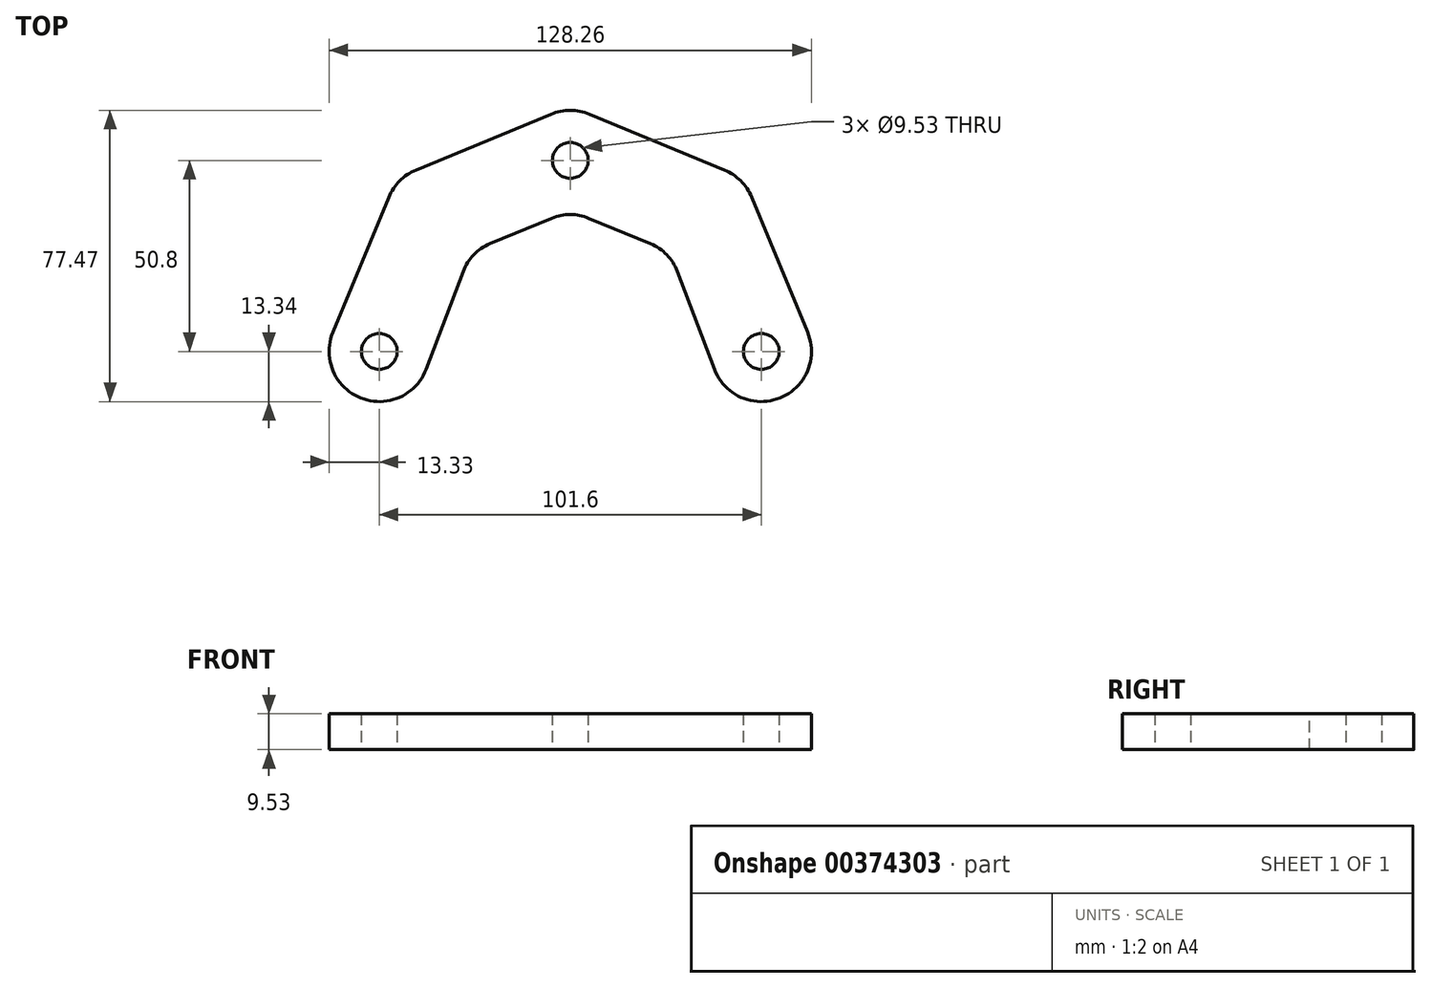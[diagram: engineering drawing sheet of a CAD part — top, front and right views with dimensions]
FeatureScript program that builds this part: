
annotation { "Feature Type Name" : "Feature", "Feature Type Description" : "" }
export const myFeature = defineFeature(function(context is Context, id is Id, definition is map)
    precondition{}
    {
        {
            var Q0;
            Q0=qCreatedBy(makeId("Top.planeOp"),FACE);
            var sketch = newSketch(context, id + "F0", { "sketchPlane" : qUnion([Q0])});
            skCircle(sketch, "E0", {"center": v(0, 0) * mm, "radius": 50.8 * mm, "construction": true});
            skLineSegment(sketch, "E1", {"start": v(0, 0) * mm, "end": v(-50.8, 0) * mm, "construction": true});
            skLineSegment(sketch, "E2", {"start": v(0, 0) * mm, "end": v(50.8, 0) * mm, "construction": true});
            skLineSegment(sketch, "E3", {"start": v(0, 37.47) * mm, "end": v(0, 50.8) * mm, "construction": true});
            skLineSegment(sketch, "E4", {"start": v(0, 0) * mm, "end": v(0, -50.8) * mm, "construction": true});
            skCircle(sketch, "E5", {"center": v(-50.8, 0) * mm, "radius": 13.34 * mm});
            skCircle(sketch, "E6", {"center": v(50.8, 0) * mm, "radius": 13.34 * mm});
            skCircle(sketch, "E7", {"center": v(50.8, 0) * mm, "radius": 4.76 * mm});
            skCircle(sketch, "E8", {"center": v(-50.8, 0) * mm, "radius": 4.76 * mm});
            skCircle(sketch, "E9", {"center": v(0, 50.8) * mm, "radius": 13.34 * mm});
            skCircle(sketch, "E10", {"center": v(0, 50.8) * mm, "radius": 4.76 * mm});
            skLineSegment(sketch, "E11", {"start": v(-26.5, 26.5) * mm, "end": v(-35.92, 35.92) * mm, "construction": true});
            skLineSegment(sketch, "E12", {"start": v(26.5, 26.5) * mm, "end": v(35.92, 35.92) * mm, "construction": true});
            skCircle(sketch, "E13", {"center": v(-35.92, 35.92) * mm, "radius": 13.34 * mm});
            skCircle(sketch, "E14", {"center": v(35.92, 35.92) * mm, "radius": 13.34 * mm});
            skLineSegment(sketch, "E15", {"start": v(63.12, 5.1) * mm, "end": v(48.24, 41.02) * mm});
            skLineSegment(sketch, "E16", {"start": v(5.1, 63.12) * mm, "end": v(41.02, 48.24) * mm});
            skLineSegment(sketch, "E17", {"start": v(-5.1, 63.12) * mm, "end": v(-41.02, 48.24) * mm});
            skLineSegment(sketch, "E18", {"start": v(-48.24, 41.02) * mm, "end": v(-63.12, 5.1) * mm});
            skLineSegment(sketch, "E19", {"start": v(-26.5, 26.5) * mm, "end": v(-38.33, -4.73) * mm});
            skLineSegment(sketch, "E20", {"start": v(-26.5, 26.5) * mm, "end": v(0, 37.47) * mm});
            skLineSegment(sketch, "E21", {"start": v(0, 37.47) * mm, "end": v(26.5, 26.5) * mm});
            skLineSegment(sketch, "E22", {"start": v(26.5, 26.5) * mm, "end": v(38.33, -4.73) * mm});
            skSolve(sketch);
        }
        {
            var Q0;
            Q0=makeQuery(id+"F0.imprint","IMPRINT",FACE,{"disambiguationData":[TD([[makeQuery(id+"F0.imprint","IMPRINT",EDGE,{"derivedFrom":sQuery(id+"F0.wireOp",EDGE,"E8")}),-1.0]])]});
            var Q1;
            {var subQ0=sQuery(id+"F0.wireOp",EDGE,"E18");Q1=makeQuery(id+"F0.imprint","IMPRINT",FACE,{"disambiguationData":[TD([[makeQuery(id+"F0.imprint","IMPRINT",EDGE,{"derivedFrom":subQ0}),1.0]])]});}
            var Q2;
            {var subQ0=sQuery(id+"F0.wireOp",EDGE,"E13");var subQ1=makeQuery(id+"F0.imprint","INTERSECT",VERTEX,{"derivedFrom":[subQ0,sQuery(id+"F0.wireOp",EDGE,"E17")]});Q2=makeQuery(id+"F0.imprint","IMPRINT",FACE,{"disambiguationData":[TD([[makeQuery(id+"F0.imprint","IMPRINT",EDGE,{"disambiguationData":[TD([[subQ1,-1.0]])],"derivedFrom":subQ0}),1.0]])]});}
            var Q3;
            {var subQ0=sQuery(id+"F0.wireOp",EDGE,"E17");Q3=makeQuery(id+"F0.imprint","IMPRINT",FACE,{"disambiguationData":[TD([[makeQuery(id+"F0.imprint","IMPRINT",EDGE,{"derivedFrom":subQ0}),1.0]])]});}
            var Q4;
            Q4=makeQuery(id+"F0.imprint","IMPRINT",FACE,{"disambiguationData":[TD([[makeQuery(id+"F0.imprint","IMPRINT",EDGE,{"derivedFrom":sQuery(id+"F0.wireOp",EDGE,"E10")}),-1.0]])]});
            var Q5;
            {var subQ0=sQuery(id+"F0.wireOp",EDGE,"E16");Q5=makeQuery(id+"F0.imprint","IMPRINT",FACE,{"disambiguationData":[TD([[makeQuery(id+"F0.imprint","IMPRINT",EDGE,{"derivedFrom":subQ0}),-1.0]])]});}
            var Q6;
            {var subQ0=sQuery(id+"F0.wireOp",EDGE,"E14");var subQ1=makeQuery(id+"F0.imprint","INTERSECT",VERTEX,{"derivedFrom":[subQ0,sQuery(id+"F0.wireOp",EDGE,"E15")]});Q6=makeQuery(id+"F0.imprint","IMPRINT",FACE,{"disambiguationData":[TD([[makeQuery(id+"F0.imprint","IMPRINT",EDGE,{"disambiguationData":[TD([[subQ1,-1.0]])],"derivedFrom":subQ0}),1.0]])]});}
            var Q7;
            {var subQ0=sQuery(id+"F0.wireOp",EDGE,"E15");Q7=makeQuery(id+"F0.imprint","IMPRINT",FACE,{"disambiguationData":[TD([[makeQuery(id+"F0.imprint","IMPRINT",EDGE,{"derivedFrom":subQ0}),1.0]])]});}
            var Q8;
            Q8=makeQuery(id+"F0.imprint","IMPRINT",FACE,{"disambiguationData":[TD([[makeQuery(id+"F0.imprint","IMPRINT",EDGE,{"derivedFrom":sQuery(id+"F0.wireOp",EDGE,"E7")}),-1.0]])]});
            extrude(context, id + "F1", {"entities" : qUnion([Q0, Q1, Q2, Q3, Q4, Q5, Q6, Q7, Q8]), "depth" : 9.52 * mm, "offsetDistance" : 25.4 * mm});
        }
        {
            var Q0;
            Q0=makeQuery(id+"F1.opExtrude","SWEPT_EDGE",EDGE,{"disambiguationData":[OSD([sQuery(id+"F0.wireOp",EDGE,"E13"),sQuery(id+"F0.wireOp",EDGE,"E19"),sQuery(id+"F0.wireOp",EDGE,"E20")])]});
            var Q1;
            Q1=makeQuery(id+"F1.opExtrude","SWEPT_EDGE",EDGE,{"disambiguationData":[OSD([sQuery(id+"F0.wireOp",EDGE,"E9"),sQuery(id+"F0.wireOp",EDGE,"E20"),sQuery(id+"F0.wireOp",EDGE,"E21")])]});
            var Q2;
            Q2=makeQuery(id+"F1.opExtrude","SWEPT_EDGE",EDGE,{"disambiguationData":[OSD([sQuery(id+"F0.wireOp",EDGE,"E14"),sQuery(id+"F0.wireOp",EDGE,"E21"),sQuery(id+"F0.wireOp",EDGE,"E22")])]});
            fillet(context, id + "F2", {"entities" : qUnion([Q0, Q1, Q2]), "radius" : 12.76 * mm, "tangentPropagation" : true, "allowEdgeOverflow" : false});
        }
    });
